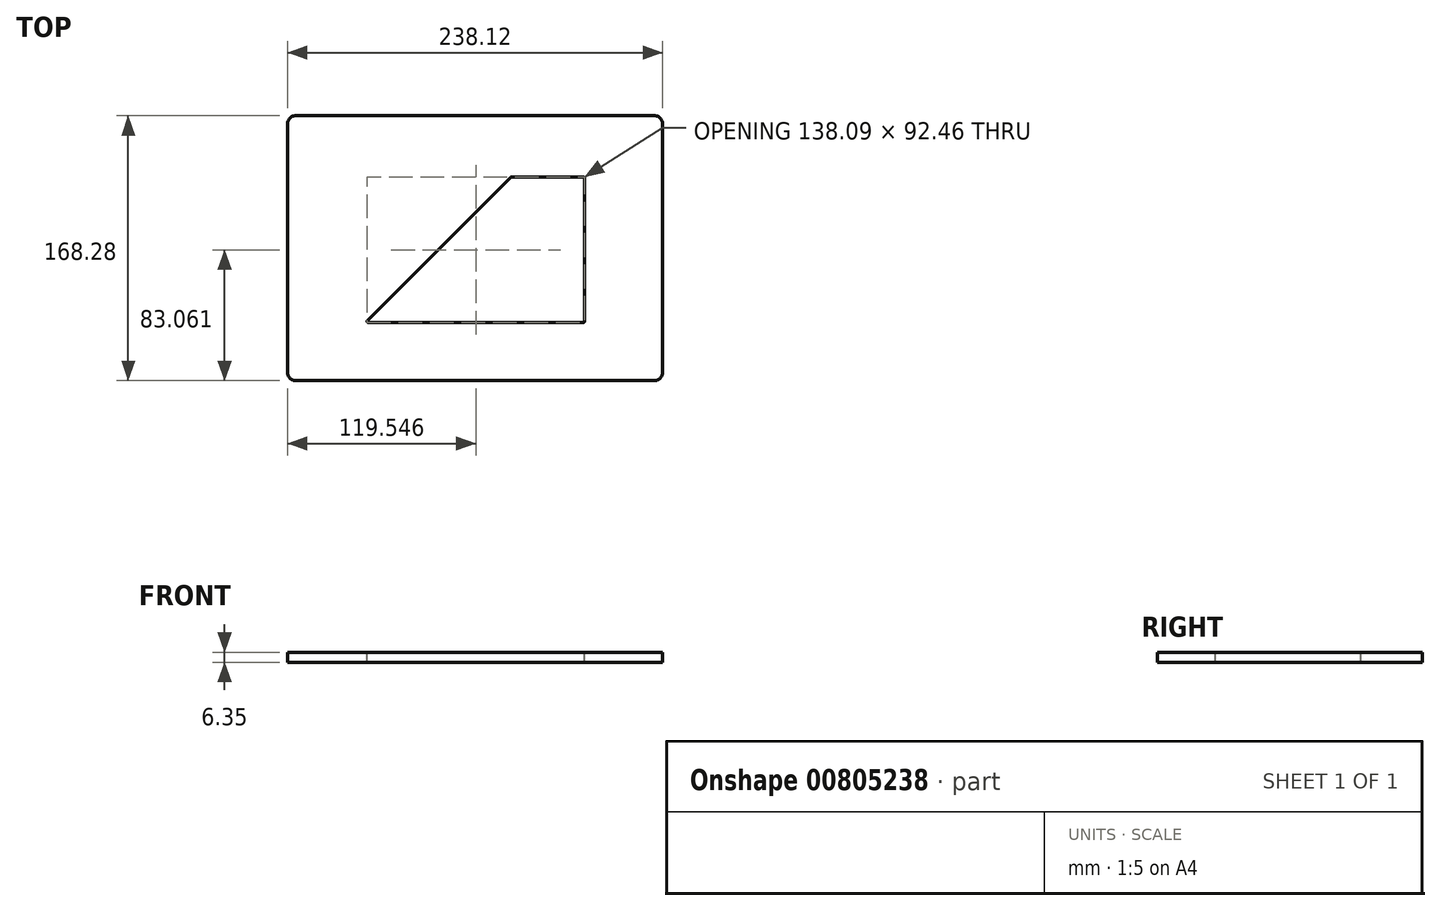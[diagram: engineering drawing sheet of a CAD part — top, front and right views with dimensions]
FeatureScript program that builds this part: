
annotation { "Feature Type Name" : "Feature", "Feature Type Description" : "" }
export const myFeature = defineFeature(function(context is Context, id is Id, definition is map)
    precondition{}
    {
        {
            var Q0;
            Q0=qCreatedBy(makeId("Top.planeOp"),FACE);
            var sketch = newSketch(context, id + "F0", { "sketchPlane" : qUnion([Q0])});
            skLineSegment(sketch, "E0.bottom", {"start": v(-119.06, 84.14) * mm, "end": v(119.06, 84.14) * mm});
            skLineSegment(sketch, "E0.top", {"start": v(-119.06, -84.14) * mm, "end": v(119.06, -84.14) * mm});
            skLineSegment(sketch, "E0.left", {"start": v(-119.06, 84.14) * mm, "end": v(-119.06, -84.14) * mm});
            skLineSegment(sketch, "E0.right", {"start": v(119.06, 84.14) * mm, "end": v(119.06, -84.14) * mm});
            skPoint(sketch, "E0.middle", {"position": v(0, 0) * mm});
            skSolve(sketch);
        }
        {
            var Q0;
            Q0 = qSketchRegion(id + "F0", true);
            extrude(context, id + "F1", {"entities" : qUnion([Q0]), "depth" : 6.35 * mm, "offsetDistance" : 25.4 * mm});
        }
        {
            var Q0;
            Q0=makeQuery(id+"F1.opExtrude","CAP_FACE",FACE,{"disambiguationData":[OSD([sQuery(id+"F0.wireOp",EDGE,"E0.bottom"),sQuery(id+"F0.wireOp",EDGE,"E0.top"),sQuery(id+"F0.wireOp",EDGE,"E0.left"),sQuery(id+"F0.wireOp",EDGE,"E0.right")])],"isStart":false});
            var sketch = newSketch(context, id + "F2", { "sketchPlane" : qUnion([Q0])});
            skLineSegment(sketch, "E1", {"start": v(-66.61, -46.04) * mm, "end": v(68.26, -46.04) * mm});
            skLineSegment(sketch, "E2", {"start": v(-66.61, -46.04) * mm, "end": v(23.3, 43.88) * mm});
            skLineSegment(sketch, "E3", {"start": v(68.26, -46.04) * mm, "end": v(68.26, 43.88) * mm});
            skLineSegment(sketch, "E4", {"start": v(23.3, 43.88) * mm, "end": v(68.26, 43.88) * mm});
            skSolve(sketch);
        }
        {
            var Q0;
            Q0 = qSketchRegion(id + "F2", true);
            extrude(context, id + "F3", {"entities" : qUnion([Q0]), "operationType" : NewBodyOperationType.REMOVE, "oppositeDirection" : true, "depth" : 25.4 * mm, "offsetDistance" : 25.4 * mm});
        }
        {
            var Q0;
            Q0=makeQuery(id+"F1.opExtrude","SWEPT_EDGE",EDGE,{"disambiguationData":[OSD([sQuery(id+"F0.wireOp",EDGE,"E0.top"),sQuery(id+"F0.wireOp",EDGE,"E0.right")])]});
            var Q1;
            Q1=makeQuery(id+"F1.opExtrude","SWEPT_EDGE",EDGE,{"disambiguationData":[OSD([sQuery(id+"F0.wireOp",EDGE,"E0.bottom"),sQuery(id+"F0.wireOp",EDGE,"E0.right")])]});
            var Q2;
            Q2=makeQuery(id+"F1.opExtrude","SWEPT_EDGE",EDGE,{"disambiguationData":[OSD([sQuery(id+"F0.wireOp",EDGE,"E0.top"),sQuery(id+"F0.wireOp",EDGE,"E0.left")])]});
            var Q3;
            Q3=makeQuery(id+"F1.opExtrude","SWEPT_EDGE",EDGE,{"disambiguationData":[OSD([sQuery(id+"F0.wireOp",EDGE,"E0.bottom"),sQuery(id+"F0.wireOp",EDGE,"E0.left")])]});
            fillet(context, id + "F4", {"entities" : qUnion([Q0, Q1, Q2, Q3]), "radius" : 5.08 * mm, "tangentPropagation" : true, "allowEdgeOverflow" : false});
        }
        {
            var Q0;
            Q0 = qSketchRegion(id + "F2", true);
            extrude(context, id + "F5", {"entities" : qUnion([Q0]), "operationType" : NewBodyOperationType.REMOVE, "endBound" : BoundingType.THROUGH_ALL, "oppositeDirection" : true, "depth" : 25.4 * mm, "offsetDistance" : 25.4 * mm});
        }
        {
            var Q0;
            Q0=makeQuery(id+"F1.opExtrude","CAP_FACE",FACE,{"disambiguationData":[OSD([sQuery(id+"F0.wireOp",EDGE,"E0.bottom"),sQuery(id+"F0.wireOp",EDGE,"E0.top"),sQuery(id+"F0.wireOp",EDGE,"E0.left"),sQuery(id+"F0.wireOp",EDGE,"E0.right")])],"isStart":false});
            var sketch = newSketch(context, id + "F6", { "sketchPlane" : qUnion([Q0])});
            skLineSegment(sketch, "E5.0", {"start": v(23.1, 45.15) * mm, "end": v(68.75, 45.15) * mm});
            skLineSegment(sketch, "E5.1", {"start": v(-68.33, -45.96) * mm, "end": v(22.55, 44.92) * mm});
            skLineSegment(sketch, "E5.2", {"start": v(-67.78, -47.3) * mm, "end": v(68.75, -47.3) * mm});
            skLineSegment(sketch, "E5.3", {"start": v(69.53, -46.52) * mm, "end": v(69.53, 44.36) * mm});
            skPoint(sketch, "E6.visualSharp", {"position": v(22.78, 45.15) * mm});
            skArc(sketch, "E6.filletArc", {"start": v(23.1, 45.15) * mm, "mid": v(22.8, 45.09) * mm, "end": v(22.55, 44.92) * mm});
            skPoint(sketch, "E7.visualSharp", {"position": v(69.53, 45.15) * mm});
            skArc(sketch, "E7.filletArc", {"start": v(69.53, 44.36) * mm, "mid": v(69.3, 44.92) * mm, "end": v(68.75, 45.15) * mm});
            skPoint(sketch, "E8.visualSharp", {"position": v(69.53, -47.3) * mm});
            skArc(sketch, "E8.filletArc", {"start": v(68.75, -47.3) * mm, "mid": v(69.3, -47.08) * mm, "end": v(69.53, -46.52) * mm});
            skPoint(sketch, "E9.visualSharp", {"position": v(-69.68, -47.3) * mm});
            skArc(sketch, "E9.filletArc", {"start": v(-68.33, -45.96) * mm, "mid": v(-68.5, -46.82) * mm, "end": v(-67.78, -47.3) * mm});
            skSolve(sketch);
        }
        {
            var Q0;
            Q0 = qSketchRegion(id + "F6", true);
            extrude(context, id + "F7", {"entities" : qUnion([Q0]), "operationType" : NewBodyOperationType.REMOVE, "endBound" : BoundingType.THROUGH_ALL, "oppositeDirection" : true, "depth" : 25.4 * mm, "offsetDistance" : 25.4 * mm});
        }
    });
